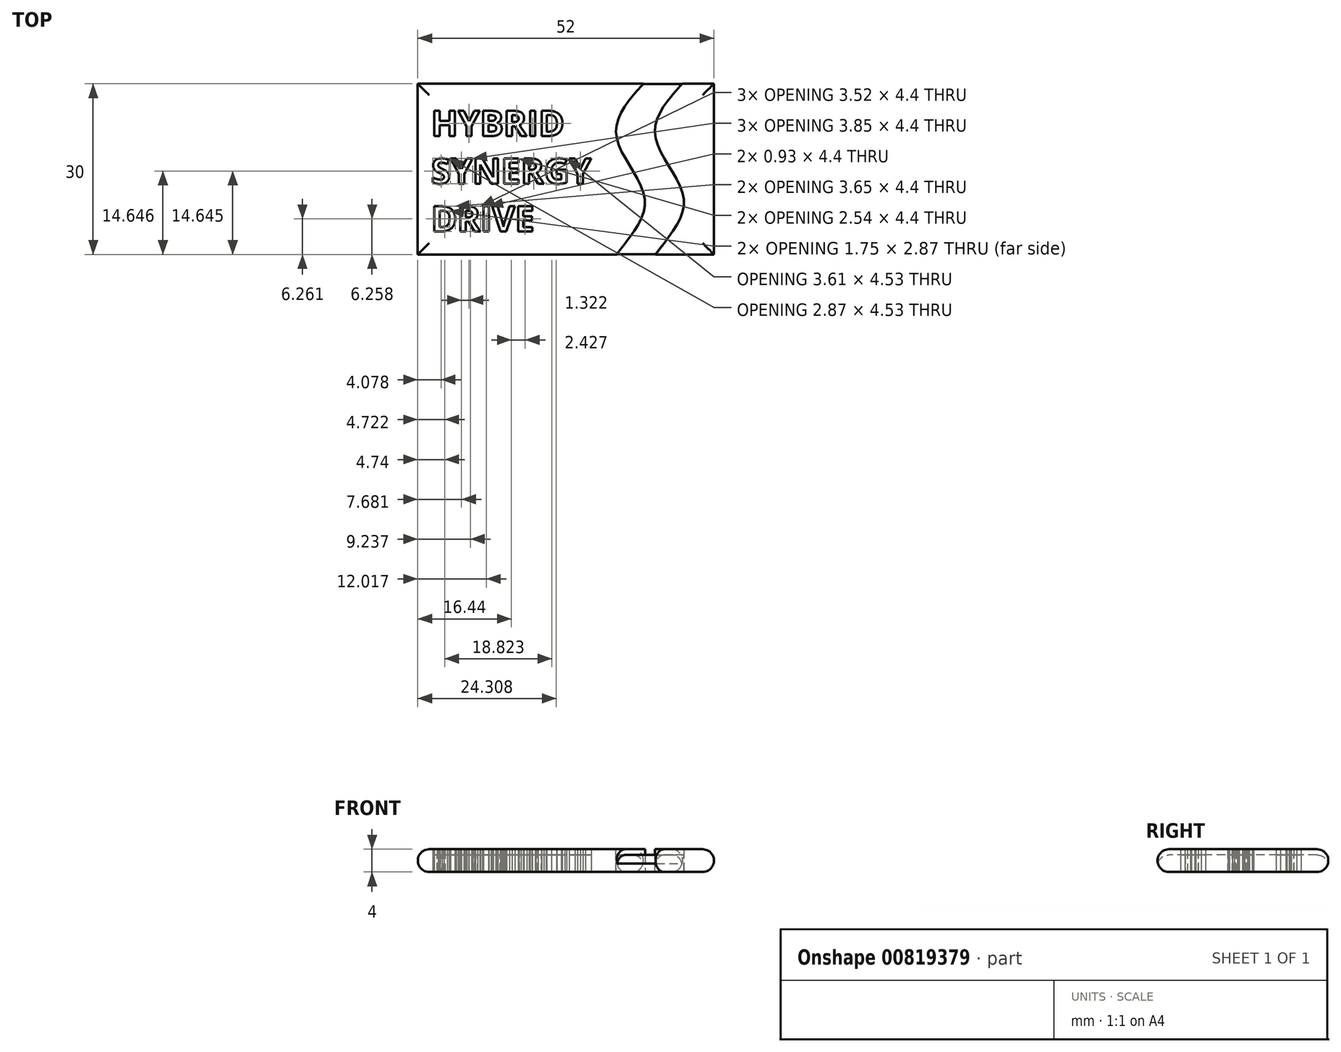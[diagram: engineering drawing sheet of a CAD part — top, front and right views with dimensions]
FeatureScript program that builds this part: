
annotation { "Feature Type Name" : "Feature", "Feature Type Description" : "" }
export const myFeature = defineFeature(function(context is Context, id is Id, definition is map)
    precondition{}
    {
        {
            var Q0;
            Q0=qCreatedBy(makeId("Top.planeOp"),FACE);
            var sketch = newSketch(context, id + "F0", { "sketchPlane" : qUnion([Q0])});
            skLineSegment(sketch, "E0.bottom", {"start": v(-25.1, 15.35) * mm, "end": v(26.9, 15.35) * mm});
            skLineSegment(sketch, "E0.top", {"start": v(-25.1, -14.65) * mm, "end": v(26.9, -14.65) * mm});
            skLineSegment(sketch, "E0.left", {"start": v(-25.1, 15.35) * mm, "end": v(-25.1, -14.65) * mm});
            skLineSegment(sketch, "E0.right", {"start": v(26.9, 15.35) * mm, "end": v(26.9, -14.65) * mm});
            skText(sketch, "E1", { "text": "HYBRID\nSYNERGY\nDRIVE", "fontName": "OpenSans-Bold.ttf"});
            skFitSpline(sketch, "E2", {"points": [v(14.5, 15.35) * mm, v(9.75, 6.21) * mm, v(14.76, -4.92) * mm, v(9.81, -14.65) * mm], "startDerivative": vector(-24.35, -26.48) * mm, "endDerivative": vector(-21.85, -29.82) * mm});
            skLineSegment(sketch, "E3", {"start": v(9.47, 15.35) * mm, "end": v(9.47, -14.65) * mm, "construction": true});
            skLineSegment(sketch, "E4", {"start": v(15.1, 15.35) * mm, "end": v(15.1, -14.65) * mm, "construction": true});
            skFitSpline(sketch, "E5", {"points": [v(21.33, 15.35) * mm, v(16.58, 6.21) * mm, v(21.58, -4.92) * mm, v(16.64, -14.65) * mm], "startDerivative": vector(-24.35, -26.48) * mm, "endDerivative": vector(-21.85, -29.82) * mm});
            const initialGuessF0  = {"E1": [-0.02274, 0.00618, 1, 0, 0.00444]};
            skSetInitialGuess(sketch, initialGuessF0);
            skSolve(sketch);
        }
        {
            var Q0;
            Q0=makeQuery(id+"F0.imprint","IMPRINT",FACE,{"disambiguationData":[TD([[makeQuery(id+"F0.imprint","IMPRINT",EDGE,{"derivedFrom":sQuery(id+"F0.wireOp",EDGE,"E1.sketch_text.stroke-65")}),-1.0]])]});
            var Q1;
            Q1=makeQuery(id+"F0.imprint","IMPRINT",FACE,{"disambiguationData":[TD([[makeQuery(id+"F0.imprint","IMPRINT",EDGE,{"derivedFrom":sQuery(id+"F0.wireOp",EDGE,"E1.sketch_text.stroke-69")}),-1.0]])]});
            var Q2;
            Q2=makeQuery(id+"F0.imprint","IMPRINT",FACE,{"disambiguationData":[TD([[makeQuery(id+"F0.imprint","IMPRINT",EDGE,{"derivedFrom":sQuery(id+"F0.wireOp",EDGE,"E1.sketch_text.stroke-46")}),-1.0]])]});
            var Q3;
            Q3=makeQuery(id+"F0.imprint","IMPRINT",FACE,{"disambiguationData":[TD([[makeQuery(id+"F0.imprint","IMPRINT",EDGE,{"derivedFrom":sQuery(id+"F0.wireOp",EDGE,"E1.sketch_text.stroke-21")}),-1.0]])]});
            var Q4;
            Q4=makeQuery(id+"F0.imprint","IMPRINT",FACE,{"disambiguationData":[TD([[makeQuery(id+"F0.imprint","IMPRINT",EDGE,{"derivedFrom":sQuery(id+"F0.wireOp",EDGE,"E1.sketch_text.stroke-12")}),-1.0]])]});
            var Q5;
            Q5=makeQuery(id+"F0.imprint","IMPRINT",FACE,{"disambiguationData":[TD([[makeQuery(id+"F0.imprint","IMPRINT",EDGE,{"derivedFrom":sQuery(id+"F0.wireOp",EDGE,"E1.sketch_text.stroke-0")}),-1.0]])]});
            var Q6;
            Q6=makeQuery(id+"F0.imprint","IMPRINT",FACE,{"disambiguationData":[TD([[makeQuery(id+"F0.imprint","IMPRINT",EDGE,{"derivedFrom":sQuery(id+"F0.wireOp",EDGE,"E1.sketch_text.stroke-81")}),-1.0]])]});
            var Q7;
            Q7=makeQuery(id+"F0.imprint","IMPRINT",FACE,{"disambiguationData":[TD([[makeQuery(id+"F0.imprint","IMPRINT",EDGE,{"derivedFrom":sQuery(id+"F0.wireOp",EDGE,"E1.sketch_text.stroke-109")}),-1.0]])]});
            var Q8;
            Q8=makeQuery(id+"F0.imprint","IMPRINT",FACE,{"disambiguationData":[TD([[makeQuery(id+"F0.imprint","IMPRINT",EDGE,{"derivedFrom":sQuery(id+"F0.wireOp",EDGE,"E1.sketch_text.stroke-118")}),-1.0]])]});
            var Q9;
            Q9=makeQuery(id+"F0.imprint","IMPRINT",FACE,{"disambiguationData":[TD([[makeQuery(id+"F0.imprint","IMPRINT",EDGE,{"derivedFrom":sQuery(id+"F0.wireOp",EDGE,"E1.sketch_text.stroke-132")}),-1.0]])]});
            var Q10;
            Q10=makeQuery(id+"F0.imprint","IMPRINT",FACE,{"disambiguationData":[TD([[makeQuery(id+"F0.imprint","IMPRINT",EDGE,{"derivedFrom":sQuery(id+"F0.wireOp",EDGE,"E1.sketch_text.stroke-144")}),-1.0]])]});
            var Q11;
            Q11=makeQuery(id+"F0.imprint","IMPRINT",FACE,{"disambiguationData":[TD([[makeQuery(id+"F0.imprint","IMPRINT",EDGE,{"derivedFrom":sQuery(id+"F0.wireOp",EDGE,"E1.sketch_text.stroke-163")}),-1.0]])]});
            var Q12;
            Q12=makeQuery(id+"F0.imprint","IMPRINT",FACE,{"disambiguationData":[TD([[makeQuery(id+"F0.imprint","IMPRINT",EDGE,{"derivedFrom":sQuery(id+"F0.wireOp",EDGE,"E1.sketch_text.stroke-182")}),-1.0]])]});
            var Q13;
            Q13=makeQuery(id+"F0.imprint","IMPRINT",FACE,{"disambiguationData":[TD([[makeQuery(id+"F0.imprint","IMPRINT",EDGE,{"derivedFrom":sQuery(id+"F0.wireOp",EDGE,"E1.sketch_text.stroke-191")}),-1.0]])]});
            var Q14;
            Q14=makeQuery(id+"F0.imprint","IMPRINT",FACE,{"disambiguationData":[TD([[makeQuery(id+"F0.imprint","IMPRINT",EDGE,{"derivedFrom":sQuery(id+"F0.wireOp",EDGE,"E1.sketch_text.stroke-203")}),-1.0]])]});
            var Q15;
            Q15=makeQuery(id+"F0.imprint","IMPRINT",FACE,{"disambiguationData":[TD([[makeQuery(id+"F0.imprint","IMPRINT",EDGE,{"derivedFrom":sQuery(id+"F0.wireOp",EDGE,"E1.sketch_text.stroke-222")}),-1.0]])]});
            var Q16;
            Q16=makeQuery(id+"F0.imprint","IMPRINT",FACE,{"disambiguationData":[TD([[makeQuery(id+"F0.imprint","IMPRINT",EDGE,{"derivedFrom":sQuery(id+"F0.wireOp",EDGE,"E1.sketch_text.stroke-226")}),-1.0]])]});
            var Q17;
            Q17=makeQuery(id+"F0.imprint","IMPRINT",FACE,{"disambiguationData":[TD([[makeQuery(id+"F0.imprint","IMPRINT",EDGE,{"derivedFrom":sQuery(id+"F0.wireOp",EDGE,"E1.sketch_text.stroke-236")}),-1.0]])]});
            var Q18;
            {var subQ0=sQuery(id+"F0.wireOp",EDGE,"E2");Q18=makeQuery(id+"F0.imprint","IMPRINT",FACE,{"disambiguationData":[TD([[makeQuery(id+"F0.imprint","IMPRINT",EDGE,{"derivedFrom":subQ0}),1.0]])]});}
            extrude(context, id + "F1", {"entities" : qUnion([Q0, Q1, Q2, Q3, Q4, Q5, Q6, Q7, Q8, Q9, Q10, Q11, Q12, Q13, Q14, Q15, Q16, Q17, Q18]), "depth" : 3 * mm, "offsetDistance" : 25 * mm});
        }
        {
            var Q0;
            {var subQ0=sQuery(id+"F0.wireOp",EDGE,"E0.left");Q0=makeQuery(id+"F0.imprint","IMPRINT",FACE,{"disambiguationData":[TD([[makeQuery(id+"F0.imprint","IMPRINT",EDGE,{"derivedFrom":subQ0}),1.0]])]});}
            var Q1;
            {var subQ0=sQuery(id+"F0.wireOp",EDGE,"E0.right");Q1=makeQuery(id+"F0.imprint","IMPRINT",FACE,{"disambiguationData":[TD([[makeQuery(id+"F0.imprint","IMPRINT",EDGE,{"derivedFrom":subQ0}),-1.0]])]});}
            var Q2;
            Q2=makeQuery(id+"F0.imprint","IMPRINT",FACE,{"disambiguationData":[TD([[makeQuery(id+"F0.imprint","IMPRINT",EDGE,{"derivedFrom":sQuery(id+"F0.wireOp",EDGE,"E1.sketch_text.stroke-76")}),1.0]])]});
            var Q3;
            Q3=makeQuery(id+"F0.imprint","IMPRINT",FACE,{"disambiguationData":[TD([[makeQuery(id+"F0.imprint","IMPRINT",EDGE,{"derivedFrom":sQuery(id+"F0.wireOp",EDGE,"E1.sketch_text.stroke-46")}),1.0]])]});
            var Q4;
            Q4=makeQuery(id+"F0.imprint","IMPRINT",FACE,{"disambiguationData":[TD([[makeQuery(id+"F0.imprint","IMPRINT",EDGE,{"derivedFrom":sQuery(id+"F0.wireOp",EDGE,"E1.sketch_text.stroke-33")}),1.0]])]});
            var Q5;
            Q5=makeQuery(id+"F0.imprint","IMPRINT",FACE,{"disambiguationData":[TD([[makeQuery(id+"F0.imprint","IMPRINT",EDGE,{"derivedFrom":sQuery(id+"F0.wireOp",EDGE,"E1.sketch_text.stroke-40")}),1.0]])]});
            var Q6;
            Q6=makeQuery(id+"F0.imprint","IMPRINT",FACE,{"disambiguationData":[TD([[makeQuery(id+"F0.imprint","IMPRINT",EDGE,{"derivedFrom":sQuery(id+"F0.wireOp",EDGE,"E1.sketch_text.stroke-144")}),1.0]])]});
            var Q7;
            Q7=makeQuery(id+"F0.imprint","IMPRINT",FACE,{"disambiguationData":[TD([[makeQuery(id+"F0.imprint","IMPRINT",EDGE,{"derivedFrom":sQuery(id+"F0.wireOp",EDGE,"E1.sketch_text.stroke-203")}),1.0]])]});
            var Q8;
            Q8=makeQuery(id+"F0.imprint","IMPRINT",FACE,{"disambiguationData":[TD([[makeQuery(id+"F0.imprint","IMPRINT",EDGE,{"derivedFrom":sQuery(id+"F0.wireOp",EDGE,"E1.sketch_text.stroke-198")}),1.0]])]});
            extrude(context, id + "F2", {"entities" : qUnion([Q0, Q1, Q2, Q3, Q4, Q5, Q6, Q7, Q8]), "depth" : 4 * mm, "offsetDistance" : 25 * mm});
        }
        {
            var Q0;
            {var subQ0=sQuery(id+"F0.wireOp",EDGE,"E0.bottom");Q0=makeQuery(id+"F2.opExtrude","CAP_EDGE",EDGE,{"disambiguationData":[OSD([subQ0]),TDD([makeQuery(id+"F0.imprint","IMPRINT",EDGE,{"disambiguationData":[TD([[makeQuery(id+"F0.imprint","INTERSECT",VERTEX,{"derivedFrom":[subQ0,sQuery(id+"F0.wireOp",EDGE,"E0.left")]}),-1.0]])],"derivedFrom":subQ0})])],"isStart":false});}
            var Q1;
            Q1=makeQuery(id+"F1.opExtrude","CAP_EDGE",EDGE,{"disambiguationData":[OSD([sQuery(id+"F0.wireOp",EDGE,"E0.bottom")])],"isStart":false});
            var Q2;
            {var subQ0=sQuery(id+"F0.wireOp",EDGE,"E0.bottom");Q2=makeQuery(id+"F2.opExtrude","CAP_EDGE",EDGE,{"disambiguationData":[OSD([subQ0]),TDD([makeQuery(id+"F0.imprint","IMPRINT",EDGE,{"disambiguationData":[TD([[makeQuery(id+"F0.imprint","INTERSECT",VERTEX,{"derivedFrom":[subQ0,sQuery(id+"F0.wireOp",EDGE,"E0.right")]}),1.0]])],"derivedFrom":subQ0})])],"isStart":false});}
            var Q3;
            {var subQ0=sQuery(id+"F0.wireOp",EDGE,"E0.top");Q3=makeQuery(id+"F2.opExtrude","CAP_EDGE",EDGE,{"disambiguationData":[OSD([subQ0]),TDD([makeQuery(id+"F0.imprint","IMPRINT",EDGE,{"disambiguationData":[TD([[makeQuery(id+"F0.imprint","INTERSECT",VERTEX,{"derivedFrom":[subQ0,sQuery(id+"F0.wireOp",EDGE,"E0.left")]}),-1.0]])],"derivedFrom":subQ0})])],"isStart":false});}
            var Q4;
            Q4=makeQuery(id+"F1.opExtrude","CAP_EDGE",EDGE,{"disambiguationData":[OSD([sQuery(id+"F0.wireOp",EDGE,"E0.top")])],"isStart":false});
            var Q5;
            {var subQ0=sQuery(id+"F0.wireOp",EDGE,"E0.top");Q5=makeQuery(id+"F2.opExtrude","CAP_EDGE",EDGE,{"disambiguationData":[OSD([subQ0]),TDD([makeQuery(id+"F0.imprint","IMPRINT",EDGE,{"disambiguationData":[TD([[makeQuery(id+"F0.imprint","INTERSECT",VERTEX,{"derivedFrom":[subQ0,sQuery(id+"F0.wireOp",EDGE,"E0.right")]}),1.0]])],"derivedFrom":subQ0})])],"isStart":false});}
            var Q6;
            Q6=makeQuery(id+"F2.opExtrude","CAP_EDGE",EDGE,{"disambiguationData":[OSD([sQuery(id+"F0.wireOp",EDGE,"E0.right")])],"isStart":false});
            var Q7;
            Q7=makeQuery(id+"F2.opExtrude","CAP_EDGE",EDGE,{"disambiguationData":[OSD([sQuery(id+"F0.wireOp",EDGE,"E0.left")])],"isStart":false});
            var Q8;
            {var subQ0=sQuery(id+"F0.wireOp",EDGE,"E0.bottom");Q8=makeQuery(id+"F2.opExtrude","CAP_EDGE",EDGE,{"disambiguationData":[OSD([subQ0]),TDD([makeQuery(id+"F0.imprint","IMPRINT",EDGE,{"disambiguationData":[TD([[makeQuery(id+"F0.imprint","INTERSECT",VERTEX,{"derivedFrom":[subQ0,sQuery(id+"F0.wireOp",EDGE,"E0.left")]}),-1.0]])],"derivedFrom":subQ0})])],"isStart":true});}
            var Q9;
            Q9=makeQuery(id+"F2.opExtrude","CAP_EDGE",EDGE,{"disambiguationData":[OSD([sQuery(id+"F0.wireOp",EDGE,"E0.left")])],"isStart":true});
            var Q10;
            Q10=makeQuery(id+"F1.opExtrude","CAP_EDGE",EDGE,{"disambiguationData":[OSD([sQuery(id+"F0.wireOp",EDGE,"E0.bottom")])],"isStart":true});
            var Q11;
            {var subQ0=sQuery(id+"F0.wireOp",EDGE,"E0.bottom");Q11=makeQuery(id+"F2.opExtrude","CAP_EDGE",EDGE,{"disambiguationData":[OSD([subQ0]),TDD([makeQuery(id+"F0.imprint","IMPRINT",EDGE,{"disambiguationData":[TD([[makeQuery(id+"F0.imprint","INTERSECT",VERTEX,{"derivedFrom":[subQ0,sQuery(id+"F0.wireOp",EDGE,"E0.right")]}),1.0]])],"derivedFrom":subQ0})])],"isStart":true});}
            var Q12;
            Q12=makeQuery(id+"F2.opExtrude","CAP_EDGE",EDGE,{"disambiguationData":[OSD([sQuery(id+"F0.wireOp",EDGE,"E0.right")])],"isStart":true});
            var Q13;
            {var subQ0=sQuery(id+"F0.wireOp",EDGE,"E0.top");Q13=makeQuery(id+"F2.opExtrude","CAP_EDGE",EDGE,{"disambiguationData":[OSD([subQ0]),TDD([makeQuery(id+"F0.imprint","IMPRINT",EDGE,{"disambiguationData":[TD([[makeQuery(id+"F0.imprint","INTERSECT",VERTEX,{"derivedFrom":[subQ0,sQuery(id+"F0.wireOp",EDGE,"E0.right")]}),1.0]])],"derivedFrom":subQ0})])],"isStart":true});}
            var Q14;
            Q14=makeQuery(id+"F1.opExtrude","CAP_EDGE",EDGE,{"disambiguationData":[OSD([sQuery(id+"F0.wireOp",EDGE,"E0.top")])],"isStart":true});
            var Q15;
            {var subQ0=sQuery(id+"F0.wireOp",EDGE,"E0.top");Q15=makeQuery(id+"F2.opExtrude","CAP_EDGE",EDGE,{"disambiguationData":[OSD([subQ0]),TDD([makeQuery(id+"F0.imprint","IMPRINT",EDGE,{"disambiguationData":[TD([[makeQuery(id+"F0.imprint","INTERSECT",VERTEX,{"derivedFrom":[subQ0,sQuery(id+"F0.wireOp",EDGE,"E0.left")]}),-1.0]])],"derivedFrom":subQ0})])],"isStart":true});}
            fillet(context, id + "F3", {"entities" : qUnion([Q0, Q1, Q2, Q3, Q4, Q5, Q6, Q7, Q8, Q9, Q10, Q11, Q12, Q13, Q14, Q15]), "radius" : 2 * mm, "tangentPropagation" : true, "allowEdgeOverflow" : false});
        }
    });
